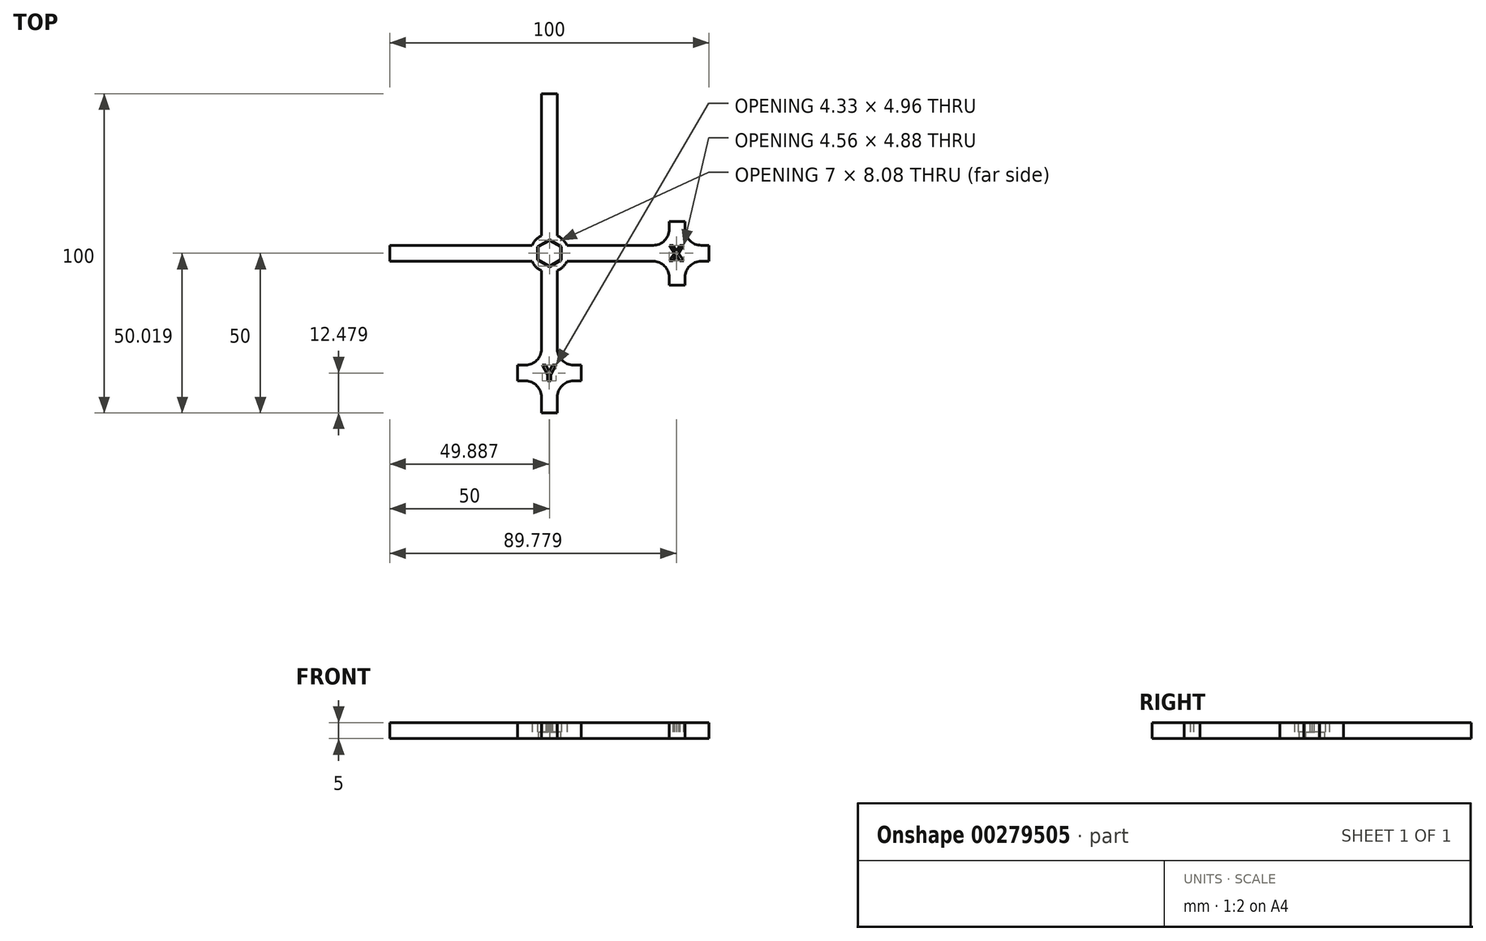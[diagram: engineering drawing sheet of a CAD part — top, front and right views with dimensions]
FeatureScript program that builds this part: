
annotation { "Feature Type Name" : "Feature", "Feature Type Description" : "" }
export const myFeature = defineFeature(function(context is Context, id is Id, definition is map)
    precondition{}
    {
        {
            var Q0;
            Q0=qCreatedBy(makeId("Top.planeOp"),FACE);
            var sketch = newSketch(context, id + "F0", { "sketchPlane" : qUnion([Q0])});
            skLineSegment(sketch, "E0.bottom", {"start": v(2.5, 50) * mm, "end": v(-2.5, 50) * mm});
            skLineSegment(sketch, "E0.top", {"start": v(2.5, -50) * mm, "end": v(-2.5, -50) * mm});
            skLineSegment(sketch, "E0.left", {"start": v(2.5, 50) * mm, "end": v(2.5, -50) * mm});
            skLineSegment(sketch, "E0.right", {"start": v(-2.5, 50) * mm, "end": v(-2.5, -50) * mm});
            skPoint(sketch, "E0.middle", {"position": v(0, 0) * mm});
            skLineSegment(sketch, "E1.bottom", {"start": v(-50, -2.5) * mm, "end": v(50, -2.5) * mm});
            skLineSegment(sketch, "E1.top", {"start": v(-50, 2.5) * mm, "end": v(50, 2.5) * mm});
            skLineSegment(sketch, "E1.left", {"start": v(-50, -2.5) * mm, "end": v(-50, 2.5) * mm});
            skLineSegment(sketch, "E1.right", {"start": v(50, -2.5) * mm, "end": v(50, 2.5) * mm});
            skCircle(sketch, "E2.cCircle", {"center": v(0, 0) * mm, "radius": 3.5 * mm, "construction": true});
            skLineSegment(sketch, "E2.0", {"start": v(0, 4.04) * mm, "end": v(3.5, 2.02) * mm});
            skLineSegment(sketch, "E2.1", {"start": v(3.5, 2.02) * mm, "end": v(3.5, -2.02) * mm});
            skLineSegment(sketch, "E2.2", {"start": v(3.5, -2.02) * mm, "end": v(0, -4.04) * mm});
            skLineSegment(sketch, "E2.3", {"start": v(0, -4.04) * mm, "end": v(-3.5, -2.02) * mm});
            skLineSegment(sketch, "E2.4", {"start": v(-3.5, -2.02) * mm, "end": v(-3.5, 2.02) * mm});
            skLineSegment(sketch, "E2.5", {"start": v(-3.5, 2.02) * mm, "end": v(0, 4.04) * mm});
            skPoint(sketch, "E2.0.midPoint", {"position": v(1.75, 3.03) * mm});
            skLineSegment(sketch, "E3.0", {"start": v(0, 4.27) * mm, "end": v(3.7, 2.14) * mm});
            skLineSegment(sketch, "E3.1", {"start": v(3.7, -2.14) * mm, "end": v(0, -4.27) * mm});
            skLineSegment(sketch, "E3.2", {"start": v(0, -4.27) * mm, "end": v(-3.7, -2.14) * mm});
            skLineSegment(sketch, "E3.3", {"start": v(3.7, 2.14) * mm, "end": v(3.7, -2.14) * mm});
            skLineSegment(sketch, "E3.4", {"start": v(-3.7, -2.14) * mm, "end": v(-3.7, 2.14) * mm});
            skLineSegment(sketch, "E3.5", {"start": v(-3.7, 2.14) * mm, "end": v(0, 4.27) * mm});
            skCircle(sketch, "E4", {"center": v(0, 0) * mm, "radius": 6 * mm});
            skLineSegment(sketch, "E5.bottom", {"start": v(10, -40) * mm, "end": v(-10, -40) * mm});
            skLineSegment(sketch, "E5.top", {"start": v(10, -35) * mm, "end": v(-10, -35) * mm});
            skLineSegment(sketch, "E5.left", {"start": v(10, -40) * mm, "end": v(10, -35) * mm});
            skLineSegment(sketch, "E5.right", {"start": v(-10, -40) * mm, "end": v(-10, -35) * mm});
            skPoint(sketch, "E5.middle", {"position": v(0, -37.5) * mm});
            skLineSegment(sketch, "E6.bottom", {"start": v(37.5, 10) * mm, "end": v(42.5, 10) * mm});
            skLineSegment(sketch, "E6.top", {"start": v(37.5, -10) * mm, "end": v(42.5, -10) * mm});
            skLineSegment(sketch, "E6.left", {"start": v(37.5, 10) * mm, "end": v(37.5, -10) * mm});
            skLineSegment(sketch, "E6.right", {"start": v(42.5, 10) * mm, "end": v(42.5, -10) * mm});
            skPoint(sketch, "E6.middle", {"position": v(40, 0) * mm});
            skText(sketch, "E7", { "text": "X", "fontName": "OpenSans-Bold.ttf"});
            skText(sketch, "E8", { "text": "Y", "fontName": "OpenSans-Bold.ttf"});
            skPoint(sketch, "E8.firstSnap0", {"position": v(0, -35) * mm});
            const initialGuessF0  = {"E7": [0.0375, -0.00242, 1, 0, 0.00492], "E8": [-0.00228, -0.04, 1, 0, 0.005]};
            skSetInitialGuess(sketch, initialGuessF0);
            skSolve(sketch);
        }
        {
            var Q0;
            Q0 = qSketchRegion(id + "F0", true);
            extrude(context, id + "F1", {"entities" : qUnion([Q0]), "depth" : 5 * mm, "offsetDistance" : 25 * mm});
        }
        {
            var Q0;
            {var subQ3=sQuery(id+"F0.wireOp",EDGE,"E0.left");var subQ9=sQuery(id+"F0.wireOp",EDGE,"E3.0");var subQ10=makeQuery(id+"F0.imprint","INTERSECT",VERTEX,{"derivedFrom":[subQ3,subQ9]});Q0=makeQuery(id+"F0.imprint","IMPRINT",FACE,{"disambiguationData":[TD([[makeQuery(id+"F0.imprint","IMPRINT",EDGE,{"disambiguationData":[TD([[subQ10,-1.0]])],"derivedFrom":subQ3}),-1.0]])]});}
            var Q1;
            {var subQ0=sQuery(id+"F0.wireOp",EDGE,"E2.4");Q1=makeQuery(id+"F0.imprint","IMPRINT",FACE,{"disambiguationData":[TD([[makeQuery(id+"F0.imprint","IMPRINT",EDGE,{"derivedFrom":subQ0}),1.0]])]});}
            var Q2;
            {var subQ0=sQuery(id+"F0.wireOp",EDGE,"E3.5");var subQ1=sQuery(id+"F0.wireOp",EDGE,"E0.right");var subQ2=makeQuery(id+"F0.imprint","INTERSECT",VERTEX,{"derivedFrom":[subQ1,subQ0]});Q2=makeQuery(id+"F0.imprint","IMPRINT",FACE,{"disambiguationData":[TD([[makeQuery(id+"F0.imprint","IMPRINT",EDGE,{"disambiguationData":[TD([[subQ2,-1.0]])],"derivedFrom":subQ1}),-1.0]])]});}
            var Q3;
            {var subQ0=sQuery(id+"F0.wireOp",EDGE,"E2.3");var subQ1=sQuery(id+"F0.wireOp",EDGE,"E0.right");var subQ2=makeQuery(id+"F0.imprint","INTERSECT",VERTEX,{"derivedFrom":[subQ1,subQ0]});Q3=makeQuery(id+"F0.imprint","IMPRINT",FACE,{"disambiguationData":[TD([[makeQuery(id+"F0.imprint","IMPRINT",EDGE,{"disambiguationData":[TD([[subQ2,-1.0]])],"derivedFrom":subQ1}),-1.0]])]});}
            var Q4;
            {var subQ1=sQuery(id+"F0.wireOp",EDGE,"E2.2");var subQ3=sQuery(id+"F0.wireOp",EDGE,"E0.left");var subQ4=makeQuery(id+"F0.imprint","INTERSECT",VERTEX,{"derivedFrom":[subQ3,subQ1]});Q4=makeQuery(id+"F0.imprint","IMPRINT",FACE,{"disambiguationData":[TD([[makeQuery(id+"F0.imprint","IMPRINT",EDGE,{"disambiguationData":[TD([[subQ4,-1.0]])],"derivedFrom":subQ3}),-1.0]])]});}
            var Q5;
            {var subQ0=sQuery(id+"F0.wireOp",EDGE,"E2.2");var subQ1=sQuery(id+"F0.wireOp",EDGE,"E0.left");var subQ2=makeQuery(id+"F0.imprint","INTERSECT",VERTEX,{"derivedFrom":[subQ1,subQ0]});Q5=makeQuery(id+"F0.imprint","IMPRINT",FACE,{"disambiguationData":[TD([[makeQuery(id+"F0.imprint","IMPRINT",EDGE,{"disambiguationData":[TD([[subQ2,-1.0]])],"derivedFrom":subQ1}),1.0]])]});}
            var Q6;
            {var subQ0=sQuery(id+"F0.wireOp",EDGE,"E2.1");Q6=makeQuery(id+"F0.imprint","IMPRINT",FACE,{"disambiguationData":[TD([[makeQuery(id+"F0.imprint","IMPRINT",EDGE,{"derivedFrom":subQ0}),1.0]])]});}
            var Q7;
            {var subQ0=sQuery(id+"F0.wireOp",EDGE,"E3.0");var subQ1=sQuery(id+"F0.wireOp",EDGE,"E0.left");var subQ2=makeQuery(id+"F0.imprint","INTERSECT",VERTEX,{"derivedFrom":[subQ1,subQ0]});Q7=makeQuery(id+"F0.imprint","IMPRINT",FACE,{"disambiguationData":[TD([[makeQuery(id+"F0.imprint","IMPRINT",EDGE,{"disambiguationData":[TD([[subQ2,-1.0]])],"derivedFrom":subQ1}),1.0]])]});}
            extrude(context, id + "F2", {"entities" : qUnion([Q0, Q1, Q2, Q3, Q4, Q5, Q6, Q7]), "operationType" : NewBodyOperationType.ADD, "depth" : 2 * mm, "offsetDistance" : 25 * mm});
        }
        {
            var Q0;
            Q0=makeQuery(id+"F1.opExtrude","SWEPT_EDGE",EDGE,{"disambiguationData":[OSD([sQuery(id+"F0.wireOp",EDGE,"E1.bottom"),sQuery(id+"F0.wireOp",EDGE,"E6.left")])]});
            var Q1;
            Q1=makeQuery(id+"F1.opExtrude","SWEPT_EDGE",EDGE,{"disambiguationData":[OSD([sQuery(id+"F0.wireOp",EDGE,"E0.right"),sQuery(id+"F0.wireOp",EDGE,"E5.bottom")])]});
            var Q2;
            Q2=makeQuery(id+"F1.opExtrude","SWEPT_EDGE",EDGE,{"disambiguationData":[OSD([sQuery(id+"F0.wireOp",EDGE,"E0.right"),sQuery(id+"F0.wireOp",EDGE,"E5.top")])]});
            var Q3;
            Q3=makeQuery(id+"F1.opExtrude","SWEPT_EDGE",EDGE,{"disambiguationData":[OSD([sQuery(id+"F0.wireOp",EDGE,"E1.top"),sQuery(id+"F0.wireOp",EDGE,"E6.left")])]});
            var Q4;
            Q4=makeQuery(id+"F1.opExtrude","SWEPT_EDGE",EDGE,{"disambiguationData":[OSD([sQuery(id+"F0.wireOp",EDGE,"E1.top"),sQuery(id+"F0.wireOp",EDGE,"E6.right")])]});
            var Q5;
            Q5=makeQuery(id+"F1.opExtrude","SWEPT_EDGE",EDGE,{"disambiguationData":[OSD([sQuery(id+"F0.wireOp",EDGE,"E0.left"),sQuery(id+"F0.wireOp",EDGE,"E5.top")])]});
            var Q6;
            Q6=makeQuery(id+"F1.opExtrude","SWEPT_EDGE",EDGE,{"disambiguationData":[OSD([sQuery(id+"F0.wireOp",EDGE,"E0.left"),sQuery(id+"F0.wireOp",EDGE,"E5.bottom")])]});
            var Q7;
            Q7=makeQuery(id+"F1.opExtrude","SWEPT_EDGE",EDGE,{"disambiguationData":[OSD([sQuery(id+"F0.wireOp",EDGE,"E1.bottom"),sQuery(id+"F0.wireOp",EDGE,"E6.right")])]});
            fillet(context, id + "F3", {"entities" : qUnion([Q0, Q1, Q2, Q3, Q4, Q5, Q6, Q7]), "radius" : 5 * mm, "tangentPropagation" : true, "allowEdgeOverflow" : false});
        }
    });
